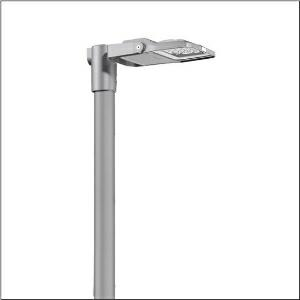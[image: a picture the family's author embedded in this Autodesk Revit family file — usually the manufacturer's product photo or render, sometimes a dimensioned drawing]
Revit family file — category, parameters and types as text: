
# Revit family: floodlight_fl_21_iq_micro___pl52_5xa7761a2d3a_8ecb
name_source: partatom
category: Lighting Fixtures
units: mm (PartAtom-declared; Revit-internal decimal feet)

## family parameters
Cut with Voids When Loaded = No
Host = Face
Light Source = No
Part Type = Normal
Room Calculation Point = No
Round Connector Dimension = Use Diameter
Shared = No

## types (1)
- --- (1 x LED, 2890 lm, 23.1 W, 3000K)
    Apparent Load = 23 VA
    CIE Flux Codes = 26 60 98 100 100
    Color Rendering = 70
    Color Temperature = 3000K
    Default Elevation = 1800 mm
    Description = Floodlight FL 21 iQ micro, floodlight, primary light control with lens, of PMMA, primary optical cover: protective disc, of toughened safety glass, transparent, light distribution: PL52, light emission: direct distribution, installation type: surface-mounted, LED, High Power LED, rated luminous flux: 2.890lm, luminous efficacy: 125lm/W, light colour: 730, colour temperature: 3000K, control gear: iQ Comfort/DALI, control: optimised constant luminous flux control (CLO 2.0), Desk-Remote (wireless, voltage-free reading and setting of iQ features in the workshop via application-optimized NFC function/RFID function), Light-Fading, Smart-Wire, Night-Set, Lumen-Switch, Temp-Guard, Auto-Match, with terminal, 6-pole, mains connection: 220..240V, AC, 50/60Hz, start of lifetime: 23W, end of service life: 24W, reduction: 11W, luminaire housing, of diecast aluminium, powder-coated, Siteco® metallic grey (DB 702S), corrosivity category C5 mid according to DIN EN ISO 12944, suitable for swimming pools, chlorine-resistant, sealing non-destructively replaceable, please order mast flange separately, mast bracket, of steel, galvanised, powder-coated, Siteco® metallic grey (DB 702S), protection rating (complete): IP66, insulation class (complete): insulation class II (safety insulation), certification: CE, ENEC, VDE, protection symbol: D, impact resistance: IK07, permissible operating ambient temperature: -40..+40°C, permissible operating ambient temperature for outdoor applications: -40..+50°C, standard: DIN EN 12944, LABS conformity tested according to VDMA 24364:2018-05, packaging unit: 1 piece

Light Distribution: PL52
    Height = 65 mm
    Lamp = 1 x LED
    Lamp Light Flux = 2890 lm
    Lamp Power = 23.1 W
    Lamp count = 1
    Length = 312 mm
    Luminous efficacy = 125 lm/W
    Manufacturer = Siteco
    ModVariant = No
    Model = 5XA7761A2D3A
    Number of Poles = 1
    OnlyDefault = Yes
    Power Factor = 1
    Product Name = Floodlight FL 21 iQ micro | PL52
    Product group = floodlight | pylon top
    ProductGroupID = 6101
    Protection Class = Protection class II
    Protection Degree = IP 66
    RLX_Detail_Level = 1
    RLX_Emergency_Light_Flux = 0 lm
    RLX_Emergency_Type = 0
    RLX_Emergency_Type_DB = No
    RlxData = <blob elided: 101973 chars, md5=8ed89e52>
    Socket = socket
    Standby Power = 0 W
    System Light Flux = 2890 lm
    System Power = 23 W
    Type Comments = factory setting: luminous flux: 100 % | dim-lin: 254 | 455 mA
    Type Image = l_1007121.jpg
    URL = http://relux.com
    VarID = @adj_178098
    Voltage = 0 V
    Weight = 0.00 kg
    Width = 230 mm

## geometry (parser evidence)
native form markers: Blend x4, Sweep x13
no freeform markers — native parametric forms only
